# Revit family: hvls_revit
name_source: partatom
category: Mechanical Equipment
revit_build: Autodesk Revit 2016 (Build: 20150220_1215(x64)
units: mm (PartAtom-declared; Revit-internal decimal feet)

## family parameters
Cut with Voids When Loaded = No
Host = Face
Part Type = Normal
Room Calculation Point = No
Round Connector Dimension = Use Diameter
Shared = No

## types (9) — shared parameters
Default Elevation = 48"
ExtPlateLength = 7 7/8"
ExtPlateWidth = 7 7/8"
ExtensionHeight = 24"
HubHeight = 21 1/2"
HubPlateLength = 12"
HubPlateWidth = 7 7/8"
HubRadius = 7"
Model = HVLS-24
MountHeight = 12"
MountPlateLength = 13 7/8"
MountPlateWidth = 7 7/8"
PlateThk = 1/4"
StemLengthWidth = 3"

## per-type parameters (varying)
| type | BladeDiameter | BladeRadius |
| HVLS-24 | 288" | 144" |
| HVLS-22 | 264" | 132" |
| HVLS-20 | 240" | 120" |
| HVLS-18 | 216" | 108" |
| HVLS-16 | 192" | 96" |
| HVLS-14 | 168" | 84" |
| HVLS-12 | 144" | 72" |
| HVLS-10 | 120" | 60" |
| HVLS-08 | 96" | 48" |

## geometry (parser evidence)
native form markers: Sweep x2
no freeform markers — native parametric forms only
